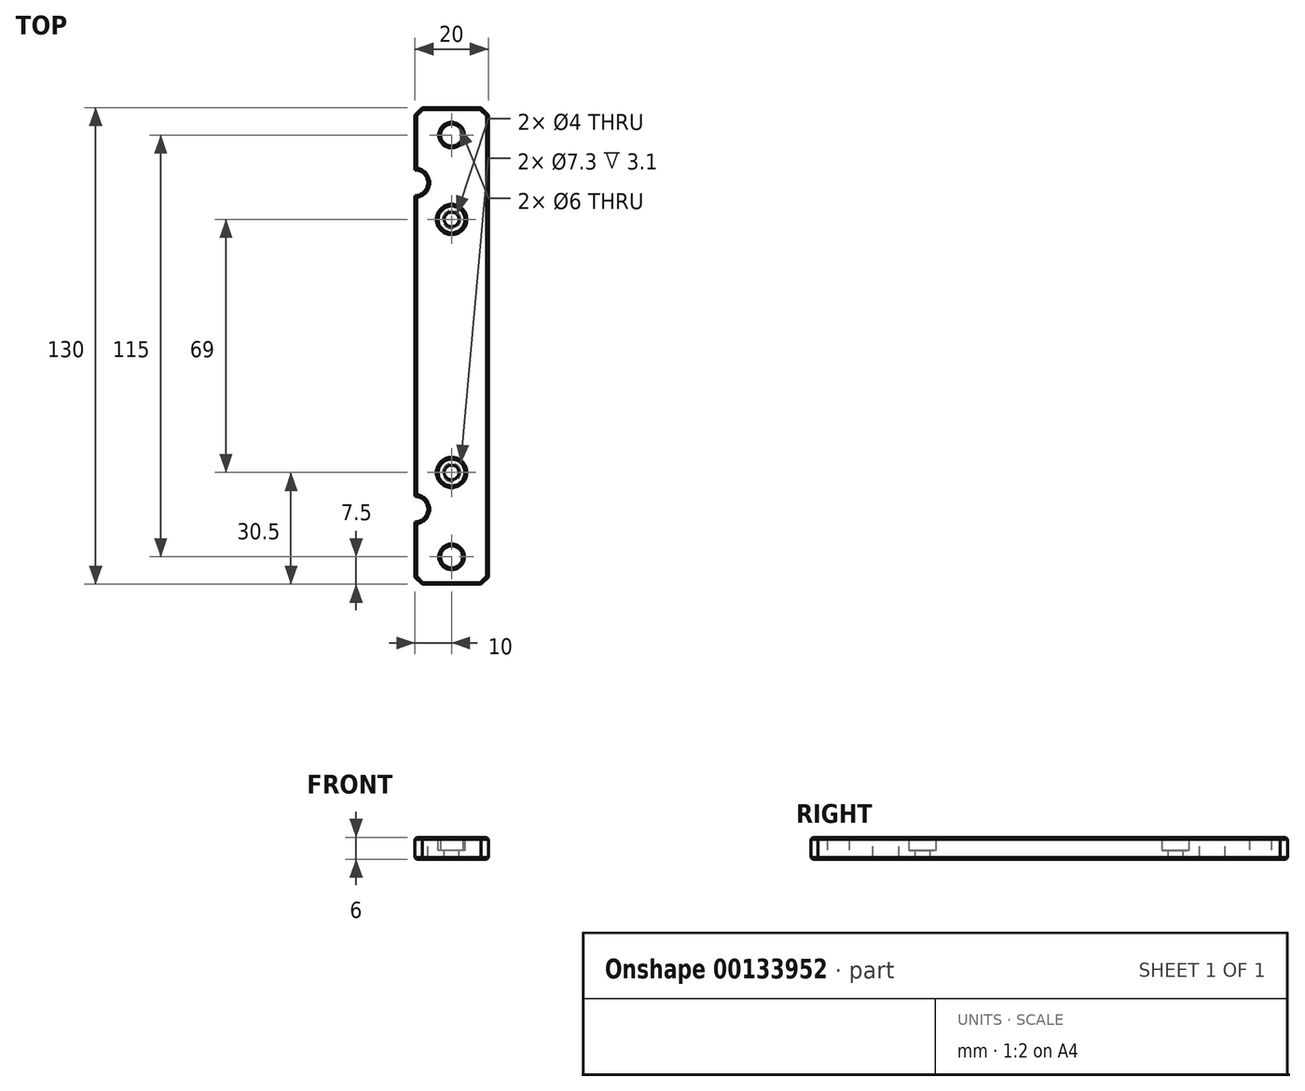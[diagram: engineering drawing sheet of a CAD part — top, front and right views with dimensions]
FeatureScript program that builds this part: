
annotation { "Feature Type Name" : "Feature", "Feature Type Description" : "" }
export const myFeature = defineFeature(function(context is Context, id is Id, definition is map)
    precondition{}
    {
        {
            var Q0;
            Q0=qCreatedBy(makeId("Top.planeOp"),FACE);
            var sketch = newSketch(context, id + "F0", { "sketchPlane" : qUnion([Q0])});
            skLineSegment(sketch, "E0.bottom", {"start": v(10, -65) * mm, "end": v(-10, -65) * mm});
            skLineSegment(sketch, "E0.top", {"start": v(10, 65) * mm, "end": v(-10, 65) * mm});
            skLineSegment(sketch, "E0.left", {"start": v(10, -65) * mm, "end": v(10, 65) * mm});
            skLineSegment(sketch, "E0.right", {"start": v(-10, -65) * mm, "end": v(-10, 65) * mm});
            skPoint(sketch, "E0.middle", {"position": v(0, 0) * mm});
            skSolve(sketch);
        }
        {
            var Q0;
            Q0 = qSketchRegion(id + "F0", true);
            extrude(context, id + "F1", {"entities" : qUnion([Q0]), "depth" : 6 * mm, "offsetDistance" : 25 * mm});
        }
        {
            var Q0;
            Q0=makeQuery(id+"F1.opExtrude","CAP_FACE",FACE,{"disambiguationData":[OSD([sQuery(id+"F0.wireOp",EDGE,"E0.bottom"),sQuery(id+"F0.wireOp",EDGE,"E0.top"),sQuery(id+"F0.wireOp",EDGE,"E0.left"),sQuery(id+"F0.wireOp",EDGE,"E0.right")])],"isStart":false});
            var sketch = newSketch(context, id + "F2", { "sketchPlane" : qUnion([Q0])});
            skPoint(sketch, "E1", {"position": v(0, 34.5) * mm});
            skPoint(sketch, "E2", {"position": v(0, -34.5) * mm});
            skSolve(sketch);
        }
        {
            var Q0;
            Q0=sQuery(id+"F2.wireOp",VERTEX,"E1");
            var Q1;
            Q1=sQuery(id+"F2.wireOp",VERTEX,"E2");
            var Q2;
            Q2=makeQuery(id+"F1.opExtrude","SWEPT_BODY",BODY,{"disambiguationData":[OSD([sQuery(id+"F0.wireOp",EDGE,"E0.bottom"),sQuery(id+"F0.wireOp",EDGE,"E0.top"),sQuery(id+"F0.wireOp",EDGE,"E0.left"),sQuery(id+"F0.wireOp",EDGE,"E0.right")])]});
            hole(context, id + "F3", {"style" : HoleStyle.C_BORE, "endStyle" : HoleEndStyle.BLIND, "holeDiameter" : 4 * mm, "cBoreDiameter" : 7.3 * mm, "cBoreDepth" : 3.6 * mm, "majorDiameter" : 5 * mm, "holeDepth" : 20 * mm, "tappedDepth" : 12 * mm, "tapClearance" : 3, "startFromSketch" : true, "locations" : qUnion([Q0, Q1]), "scope" : qUnion([Q2])});
        }
        {
            var Q0;
            Q0=makeQuery(id+"F1.opExtrude","CAP_FACE",FACE,{"disambiguationData":[OSD([sQuery(id+"F0.wireOp",EDGE,"E0.bottom"),sQuery(id+"F0.wireOp",EDGE,"E0.top"),sQuery(id+"F0.wireOp",EDGE,"E0.left"),sQuery(id+"F0.wireOp",EDGE,"E0.right")])],"isStart":false});
            var sketch = newSketch(context, id + "F4", { "sketchPlane" : qUnion([Q0])});
            skPoint(sketch, "E3", {"position": v(-10, 44.5) * mm});
            skPoint(sketch, "E4", {"position": v(-10, -44.5) * mm});
            skSolve(sketch);
        }
        {
            var Q0;
            Q0=sQuery(id+"F4.wireOp",VERTEX,"E3");
            var Q1;
            Q1=sQuery(id+"F4.wireOp",VERTEX,"E4");
            var Q2;
            Q2=makeQuery(id+"F1.opExtrude","SWEPT_BODY",BODY,{"disambiguationData":[OSD([sQuery(id+"F0.wireOp",EDGE,"E0.bottom"),sQuery(id+"F0.wireOp",EDGE,"E0.top"),sQuery(id+"F0.wireOp",EDGE,"E0.left"),sQuery(id+"F0.wireOp",EDGE,"E0.right")])]});
            hole(context, id + "F5", {"style" : HoleStyle.SIMPLE, "endStyle" : HoleEndStyle.BLIND, "holeDiameter" : 7 * mm, "majorDiameter" : 5 * mm, "holeDepth" : 20 * mm, "tappedDepth" : 12 * mm, "tapClearance" : 3, "startFromSketch" : true, "locations" : qUnion([Q0, Q1]), "scope" : qUnion([Q2])});
        }
        {
            var Q0;
            Q0=makeQuery(id+"F1.opExtrude","CAP_FACE",FACE,{"disambiguationData":[OSD([sQuery(id+"F0.wireOp",EDGE,"E0.bottom"),sQuery(id+"F0.wireOp",EDGE,"E0.top"),sQuery(id+"F0.wireOp",EDGE,"E0.left"),sQuery(id+"F0.wireOp",EDGE,"E0.right")])],"isStart":true});
            var sketch = newSketch(context, id + "F6", { "sketchPlane" : qUnion([Q0])});
            skPoint(sketch, "E5", {"position": v(0, -57.5) * mm});
            skPoint(sketch, "E6", {"position": v(0, 57.5) * mm});
            skSolve(sketch);
        }
        {
            var Q0;
            Q0=sQuery(id+"F6.wireOp",VERTEX,"E5");
            var Q1;
            Q1=sQuery(id+"F6.wireOp",VERTEX,"E6");
            var Q2;
            Q2=makeQuery(id+"F1.opExtrude","SWEPT_BODY",BODY,{"disambiguationData":[OSD([sQuery(id+"F0.wireOp",EDGE,"E0.bottom"),sQuery(id+"F0.wireOp",EDGE,"E0.top"),sQuery(id+"F0.wireOp",EDGE,"E0.left"),sQuery(id+"F0.wireOp",EDGE,"E0.right")])]});
            hole(context, id + "F7", {"style" : HoleStyle.SIMPLE, "endStyle" : HoleEndStyle.BLIND, "holeDiameter" : 6 * mm, "majorDiameter" : 5 * mm, "holeDepth" : 20 * mm, "tappedDepth" : 12 * mm, "tapClearance" : 3, "startFromSketch" : true, "locations" : qUnion([Q0, Q1]), "scope" : qUnion([Q2])});
        }
        {
            var Q0;
            Q0=makeQuery(id+"F1.opExtrude","SWEPT_EDGE",EDGE,{"disambiguationData":[OSD([sQuery(id+"F0.wireOp",EDGE,"E0.bottom"),sQuery(id+"F0.wireOp",EDGE,"E0.right")])]});
            var Q1;
            Q1=makeQuery(id+"F1.opExtrude","SWEPT_EDGE",EDGE,{"disambiguationData":[OSD([sQuery(id+"F0.wireOp",EDGE,"E0.bottom"),sQuery(id+"F0.wireOp",EDGE,"E0.left")])]});
            var Q2;
            Q2=makeQuery(id+"F1.opExtrude","SWEPT_EDGE",EDGE,{"disambiguationData":[OSD([sQuery(id+"F0.wireOp",EDGE,"E0.top"),sQuery(id+"F0.wireOp",EDGE,"E0.right")])]});
            var Q3;
            Q3=makeQuery(id+"F1.opExtrude","SWEPT_EDGE",EDGE,{"disambiguationData":[OSD([sQuery(id+"F0.wireOp",EDGE,"E0.top"),sQuery(id+"F0.wireOp",EDGE,"E0.left")])]});
            chamfer(context, id + "F8", {"entities" : qUnion([Q0, Q1, Q2, Q3]), "width" : 2 * mm, "tangentPropagation" : true});
        }
        {
            var Q0;
            Q0=makeQuery(id+"F1.opExtrude","CAP_FACE",FACE,{"disambiguationData":[OSD([sQuery(id+"F0.wireOp",EDGE,"E0.bottom"),sQuery(id+"F0.wireOp",EDGE,"E0.top"),sQuery(id+"F0.wireOp",EDGE,"E0.left"),sQuery(id+"F0.wireOp",EDGE,"E0.right")])],"isStart":true});
            var Q1;
            Q1=makeQuery(id+"F1.opExtrude","CAP_FACE",FACE,{"disambiguationData":[OSD([sQuery(id+"F0.wireOp",EDGE,"E0.bottom"),sQuery(id+"F0.wireOp",EDGE,"E0.top"),sQuery(id+"F0.wireOp",EDGE,"E0.left"),sQuery(id+"F0.wireOp",EDGE,"E0.right")])],"isStart":false});
            chamfer(context, id + "F9", {"entities" : qUnion([Q0, Q1]), "width" : 0.5 * mm, "tangentPropagation" : true});
        }
    });
